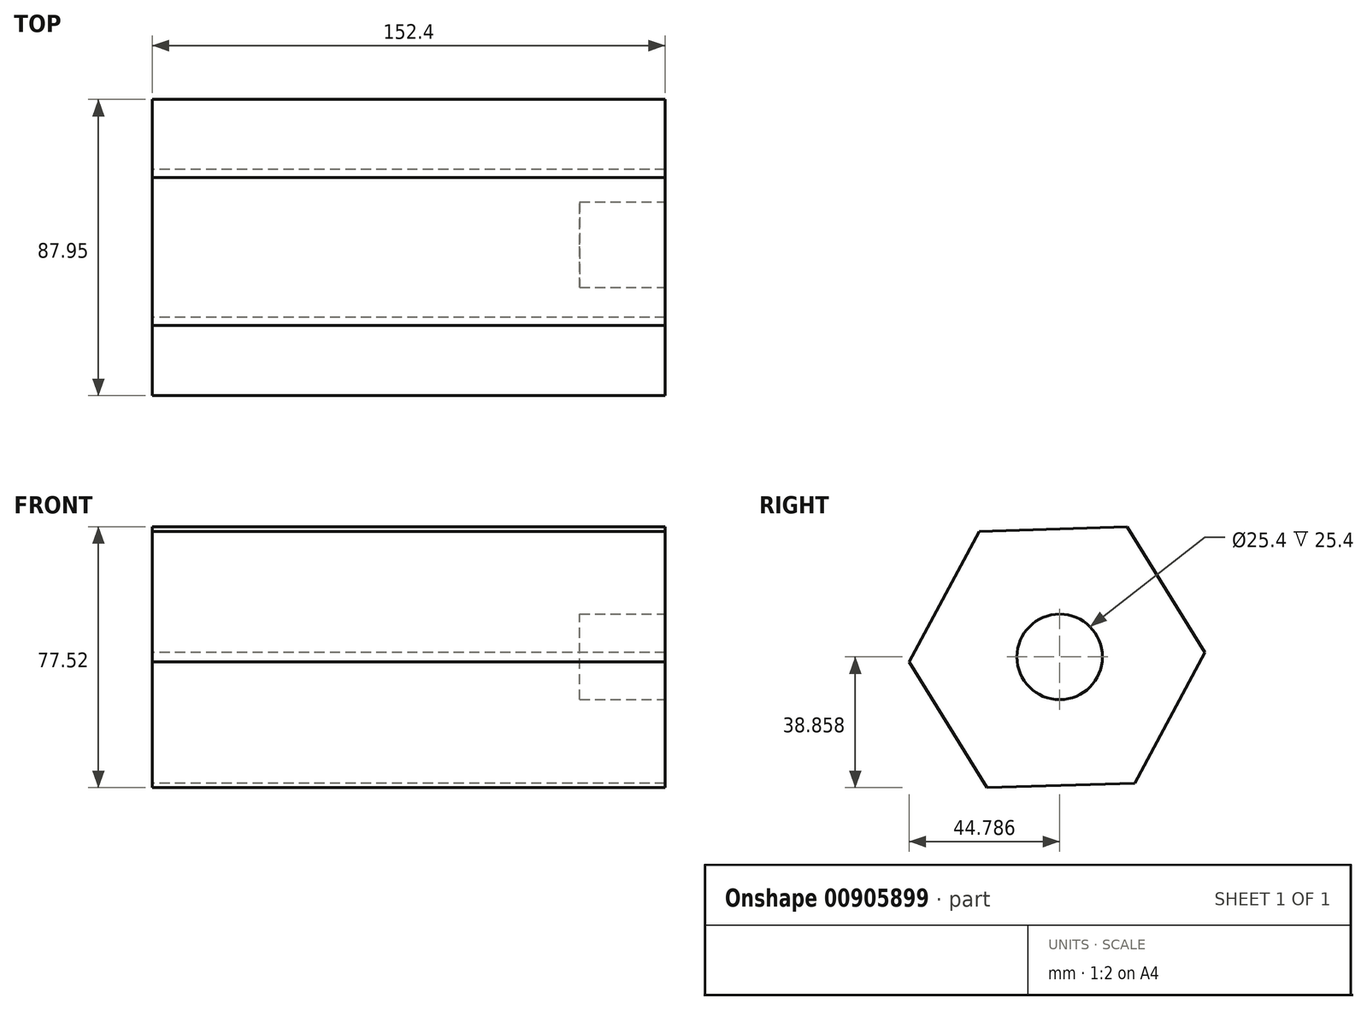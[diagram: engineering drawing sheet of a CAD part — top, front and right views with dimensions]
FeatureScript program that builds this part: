
annotation { "Feature Type Name" : "Feature", "Feature Type Description" : "" }
export const myFeature = defineFeature(function(context is Context, id is Id, definition is map)
    precondition{}
    {
        {
            var Q0;
            Q0=qCreatedBy(makeId("Right.planeOp"),FACE);
            var sketch = newSketch(context, id + "F0", { "sketchPlane" : qUnion([Q0])});
            skCircle(sketch, "E0.cCircle", {"center": v(-3.01, 66.77) * mm, "radius": 38.1 * mm, "construction": true});
            skLineSegment(sketch, "E0.0", {"start": v(48.83, 94.04) * mm, "end": v(28.03, 55.28) * mm});
            skLineSegment(sketch, "E0.1", {"start": v(20.15, 29.37) * mm, "end": v(-23.82, 28) * mm});
            skLineSegment(sketch, "E0.2", {"start": v(-23.82, 28) * mm, "end": v(-46.99, 65.4) * mm});
            skLineSegment(sketch, "E0.3", {"start": v(-46.99, 65.4) * mm, "end": v(-26.18, 104.17) * mm});
            skLineSegment(sketch, "E0.4", {"start": v(-26.18, 104.17) * mm, "end": v(17.8, 105.53) * mm});
            skLineSegment(sketch, "E0.5", {"start": v(17.8, 105.53) * mm, "end": v(40.96, 68.13) * mm});
            skPoint(sketch, "E0.0.midPoint", {"position": v(30.56, 48.75) * mm});
            skCircle(sketch, "E1.0.1.0", {"center": v(-3.01, -85.63) * mm, "radius": 38.1 * mm, "construction": true});
            skLineSegment(sketch, "E1.0.1.1", {"start": v(40.96, -84.27) * mm, "end": v(20.15, -123.03) * mm});
            skLineSegment(sketch, "E1.0.1.2", {"start": v(20.15, -123.03) * mm, "end": v(-23.82, -124.4) * mm});
            skLineSegment(sketch, "E1.0.1.3", {"start": v(-23.82, -124.4) * mm, "end": v(-46.99, -87) * mm});
            skLineSegment(sketch, "E1.0.1.4", {"start": v(-46.99, -87) * mm, "end": v(-26.18, -48.23) * mm});
            skLineSegment(sketch, "E1.0.1.5", {"start": v(-26.18, -48.23) * mm, "end": v(17.8, -46.87) * mm});
            skLineSegment(sketch, "E1.0.1.6", {"start": v(17.8, -46.87) * mm, "end": v(40.96, -84.27) * mm});
            skLineSegment(sketch, "E1.direction1", {"start": v(-3.01, 66.77) * mm, "end": v(16.58, 66.77) * mm, "construction": true});
            skLineSegment(sketch, "E1.direction2", {"start": v(-3.01, 66.77) * mm, "end": v(-3.01, -85.63) * mm, "construction": true});
            skSolve(sketch);
        }
        {
            var Q0;
            Q0 = qSketchRegion(id + "F0", true);
            extrude(context, id + "F1", {"entities" : qUnion([Q0]), "depth" : 152.4 * mm, "offsetDistance" : 25.4 * mm});
        }
        {
            var Q0;
            Q0=makeQuery(id+"F1.opExtrude","CAP_FACE",FACE,{"disambiguationData":[OSD([sQuery(id+"F0.wireOp",EDGE,"E1.0.1.1"),sQuery(id+"F0.wireOp",EDGE,"E1.0.1.2"),sQuery(id+"F0.wireOp",EDGE,"E1.0.1.3"),sQuery(id+"F0.wireOp",EDGE,"E1.0.1.4"),sQuery(id+"F0.wireOp",EDGE,"E1.0.1.5"),sQuery(id+"F0.wireOp",EDGE,"E1.0.1.6")])],"isStart":false});
            var sketch = newSketch(context, id + "F2", { "sketchPlane" : qUnion([Q0])});
            skCircle(sketch, "E2", {"center": v(-2.2, -85.53) * mm, "radius": 12.7 * mm});
            skSolve(sketch);
        }
        {
            var Q0;
            Q0 = qSketchRegion(id + "F2", true);
            extrude(context, id + "F3", {"entities" : qUnion([Q0]), "operationType" : NewBodyOperationType.REMOVE, "oppositeDirection" : true, "depth" : 25.4 * mm, "offsetDistance" : 25.4 * mm});
        }
    });
